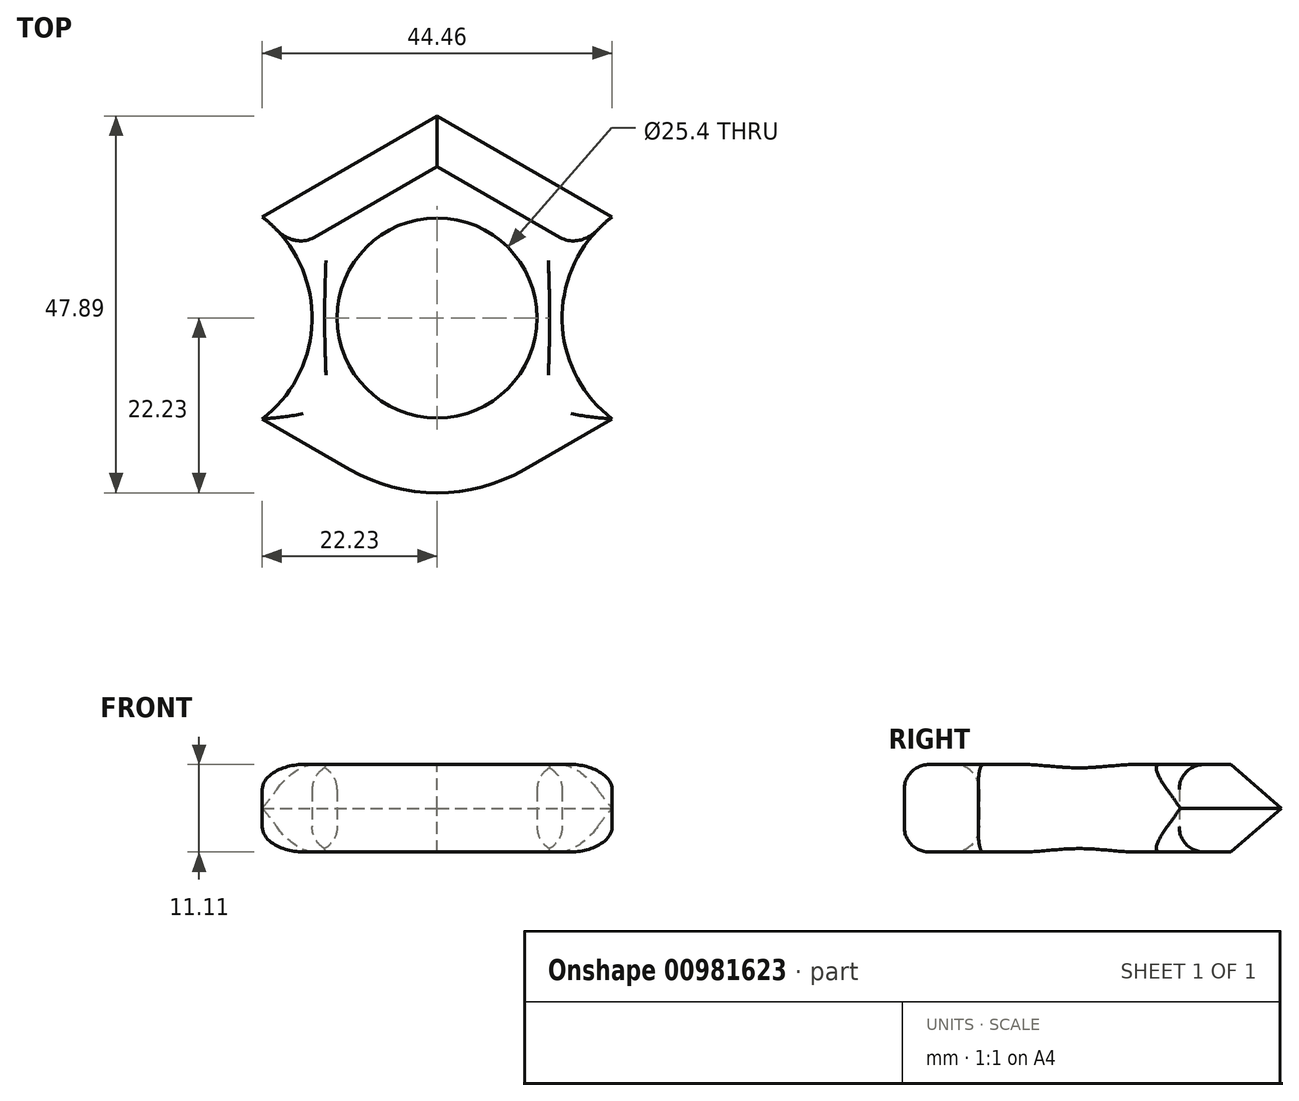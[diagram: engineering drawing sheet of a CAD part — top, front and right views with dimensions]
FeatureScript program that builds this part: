
annotation { "Feature Type Name" : "Feature", "Feature Type Description" : "" }
export const myFeature = defineFeature(function(context is Context, id is Id, definition is map)
    precondition{}
    {
        {
            var Q0;
            Q0=qCreatedBy(makeId("Top.planeOp"),FACE);
            var sketch = newSketch(context, id + "F0", { "sketchPlane" : qUnion([Q0])});
            skCircle(sketch, "E0", {"center": v(0, 0) * mm, "radius": 12.7 * mm});
            skCircle(sketch, "E1.cCircle", {"center": v(0, 0) * mm, "radius": 22.23 * mm, "construction": true});
            skLineSegment(sketch, "E1.0", {"start": v(-22.23, -12.83) * mm, "end": v(-22.23, 12.83) * mm, "construction": true});
            skLineSegment(sketch, "E1.1", {"start": v(-22.23, 12.83) * mm, "end": v(0, 25.66) * mm});
            skLineSegment(sketch, "E1.2", {"start": v(0, 25.66) * mm, "end": v(22.23, 12.83) * mm});
            skLineSegment(sketch, "E1.3", {"start": v(22.23, 12.83) * mm, "end": v(22.23, -12.83) * mm, "construction": true});
            skLineSegment(sketch, "E1.4", {"start": v(22.23, -12.83) * mm, "end": v(0, -25.66) * mm});
            skLineSegment(sketch, "E1.5", {"start": v(0, -25.66) * mm, "end": v(-22.22, -12.83) * mm});
            skPoint(sketch, "E1.0.midPoint", {"position": v(-22.22, 0) * mm});
            skArc(sketch, "E2", {"start": v(-22.23, -12.83) * mm, "mid": v(-15.88, 0) * mm, "end": v(-22.23, 12.83) * mm});
            skArc(sketch, "E3", {"start": v(22.23, 12.83) * mm, "mid": v(15.88, 0) * mm, "end": v(22.23, -12.83) * mm});
            skArc(sketch, "E4", {"start": v(-11.11, -19.25) * mm, "mid": v(0, -22.22) * mm, "end": v(11.11, -19.25) * mm});
            skSolve(sketch);
        }
        {
            var Q0;
            Q0=makeQuery(id+"F0.imprint","IMPRINT",FACE,{"disambiguationData":[TD([[makeQuery(id+"F0.imprint","IMPRINT",EDGE,{"derivedFrom":sQuery(id+"F0.wireOp",EDGE,"E0")}),-1.0]])]});
            extrude(context, id + "F1", {"entities" : qUnion([Q0]), "depth" : 11.1 * mm, "offsetDistance" : 25.4 * mm});
        }
        {
            var Q0;
            Q0=makeQuery(id+"F1.opExtrude","CAP_EDGE",EDGE,{"disambiguationData":[OSD([sQuery(id+"F0.wireOp",EDGE,"E1.2")])],"isStart":true});
            var Q1;
            Q1=makeQuery(id+"F1.opExtrude","CAP_EDGE",EDGE,{"disambiguationData":[OSD([sQuery(id+"F0.wireOp",EDGE,"E1.2")])],"isStart":false});
            var Q2;
            Q2=makeQuery(id+"F1.opExtrude","CAP_EDGE",EDGE,{"disambiguationData":[OSD([sQuery(id+"F0.wireOp",EDGE,"E1.1")])],"isStart":false});
            var Q3;
            Q3=makeQuery(id+"F1.opExtrude","CAP_EDGE",EDGE,{"disambiguationData":[OSD([sQuery(id+"F0.wireOp",EDGE,"E1.1")])],"isStart":true});
            chamfer(context, id + "F2", {"entities" : qUnion([Q0, Q1, Q2, Q3]), "width" : 5.56 * mm, "tangentPropagation" : true});
        }
        {
            var Q0;
            Q0=makeQuery(id+"F1.opExtrude","SWEPT_FACE",FACE,{"disambiguationData":[OSD([sQuery(id+"F0.wireOp",EDGE,"E0")])]});
            var Q1;
            Q1=makeQuery(id+"F1.opExtrude","CAP_EDGE",EDGE,{"disambiguationData":[OSD([sQuery(id+"F0.wireOp",EDGE,"E2")])],"isStart":false});
            var Q2;
            Q2=makeQuery(id+"F1.opExtrude","CAP_EDGE",EDGE,{"disambiguationData":[OSD([sQuery(id+"F0.wireOp",EDGE,"E2")])],"isStart":true});
            var Q3;
            Q3=makeQuery(id+"F1.opExtrude","CAP_EDGE",EDGE,{"disambiguationData":[OSD([sQuery(id+"F0.wireOp",EDGE,"E1.5")])],"isStart":false});
            var Q4;
            Q4=makeQuery(id+"F1.opExtrude","CAP_EDGE",EDGE,{"disambiguationData":[OSD([sQuery(id+"F0.wireOp",EDGE,"E1.5")])],"isStart":true});
            var Q5;
            Q5=makeQuery(id+"F1.opExtrude","CAP_EDGE",EDGE,{"disambiguationData":[OSD([sQuery(id+"F0.wireOp",EDGE,"E4")])],"isStart":false});
            var Q6;
            Q6=makeQuery(id+"F1.opExtrude","CAP_EDGE",EDGE,{"disambiguationData":[OSD([sQuery(id+"F0.wireOp",EDGE,"E4")])],"isStart":true});
            var Q7;
            Q7=makeQuery(id+"F1.opExtrude","CAP_EDGE",EDGE,{"disambiguationData":[OSD([sQuery(id+"F0.wireOp",EDGE,"E1.4")])],"isStart":true});
            var Q8;
            Q8=makeQuery(id+"F1.opExtrude","CAP_EDGE",EDGE,{"disambiguationData":[OSD([sQuery(id+"F0.wireOp",EDGE,"E1.4")])],"isStart":false});
            var Q9;
            Q9=makeQuery(id+"F1.opExtrude","CAP_EDGE",EDGE,{"disambiguationData":[OSD([sQuery(id+"F0.wireOp",EDGE,"E3")])],"isStart":true});
            var Q10;
            Q10=makeQuery(id+"F1.opExtrude","CAP_EDGE",EDGE,{"disambiguationData":[OSD([sQuery(id+"F0.wireOp",EDGE,"E3")])],"isStart":false});
            fillet(context, id + "F3", {"entities" : qUnion([Q0, Q1, Q2, Q3, Q4, Q5, Q6, Q7, Q8, Q9, Q10]), "radius" : 3.17 * mm, "tangentPropagation" : true, "allowEdgeOverflow" : false});
        }
    });
